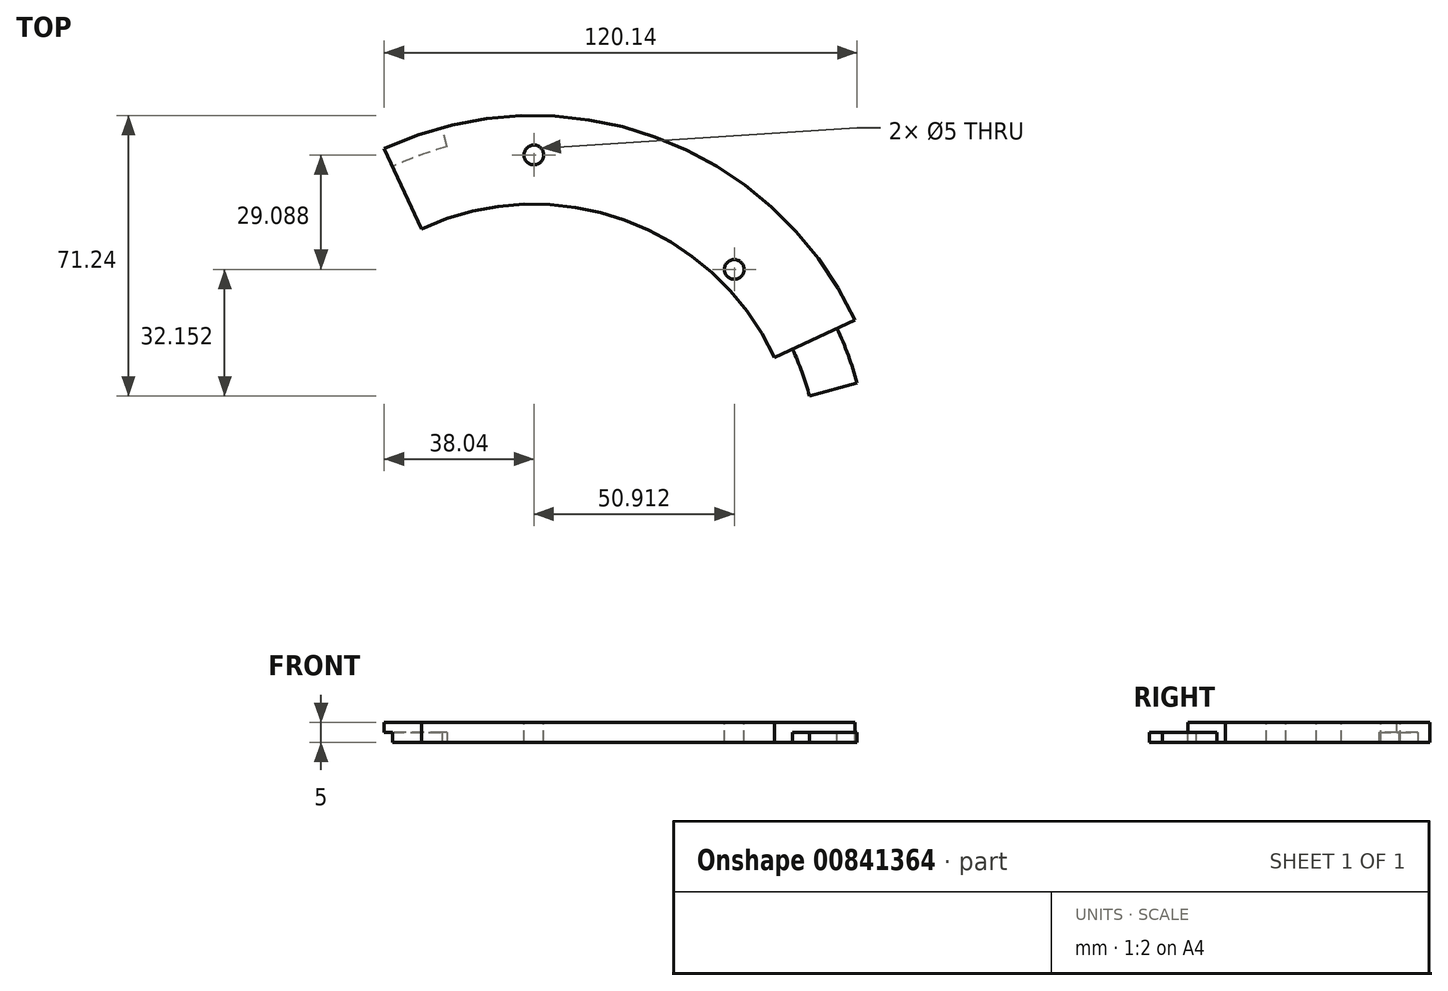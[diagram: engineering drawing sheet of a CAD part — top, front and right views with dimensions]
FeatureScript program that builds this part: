
annotation { "Feature Type Name" : "Feature", "Feature Type Description" : "" }
export const myFeature = defineFeature(function(context is Context, id is Id, definition is map)
    precondition{}
    {
        {
            var Q0;
            Q0=qCreatedBy(makeId("Top.planeOp"),FACE);
            var sketch = newSketch(context, id + "F0", { "sketchPlane" : qUnion([Q0])});
            skCircle(sketch, "E0", {"center": v(0, 0) * mm, "radius": 90 * mm});
            skSolve(sketch);
        }
        {
            var Q0;
            Q0 = qSketchRegion(id + "F0", true);
            extrude(context, id + "F1", {"entities" : qUnion([Q0]), "depth" : 5 * mm, "offsetDistance" : 25 * mm});
        }
        {
            var Q0;
            Q0=makeQuery(id+"F1.opExtrude","CAP_FACE",FACE,{"disambiguationData":[OSD([sQuery(id+"F0.wireOp",EDGE,"E0")])],"isStart":false});
            var sketch = newSketch(context, id + "F2", { "sketchPlane" : qUnion([Q0])});
            skCircle(sketch, "E1", {"center": v(0, 0) * mm, "radius": 67.5 * mm});
            skSolve(sketch);
        }
        {
            var Q0;
            Q0 = qSketchRegion(id + "F2", true);
            extrude(context, id + "F3", {"entities" : qUnion([Q0]), "operationType" : NewBodyOperationType.REMOVE, "oppositeDirection" : true, "depth" : 5 * mm, "offsetDistance" : 25 * mm});
        }
        {
            var Q0;
            Q0=makeQuery(id+"F1.opExtrude","CAP_FACE",FACE,{"disambiguationData":[OSD([sQuery(id+"F0.wireOp",EDGE,"E0")])],"isStart":false});
            var sketch = newSketch(context, id + "F4", { "sketchPlane" : qUnion([Q0])});
            skCircle(sketch, "E2", {"center": v(0, 80) * mm, "radius": 2.5 * mm});
            skSolve(sketch);
        }
        {
            var Q0;
            Q0 = qSketchRegion(id + "F4", true);
            extrude(context, id + "F5", {"entities" : qUnion([Q0]), "operationType" : NewBodyOperationType.REMOVE, "endBound" : BoundingType.THROUGH_ALL, "oppositeDirection" : true, "depth" : 25 * mm, "offsetDistance" : 25 * mm});
        }
        {
            var Q0;
            Q0=makeQuery(id+"F1.opExtrude","CAP_FACE",FACE,{"disambiguationData":[OSD([sQuery(id+"F0.wireOp",EDGE,"E0")])],"isStart":false});
            var sketch = newSketch(context, id + "F6", { "sketchPlane" : qUnion([Q0])});
            skCircle(sketch, "E3", {"center": v(50.91, 50.91) * mm, "radius": 2.5 * mm});
            skLineSegment(sketch, "E4", {"start": v(50.91, 50.91) * mm, "end": v(0, 0) * mm});
            skSolve(sketch);
        }
        {
            var Q0;
            Q0 = qSketchRegion(id + "F6", true);
            extrude(context, id + "F7", {"entities" : qUnion([Q0]), "operationType" : NewBodyOperationType.REMOVE, "endBound" : BoundingType.THROUGH_ALL, "oppositeDirection" : true, "depth" : 25 * mm, "offsetDistance" : 25 * mm});
        }
        {
            var Q0;
            Q0=makeQuery(id+"F1.opExtrude","CAP_FACE",FACE,{"disambiguationData":[OSD([sQuery(id+"F0.wireOp",EDGE,"E0")])],"isStart":false});
            var sketch = newSketch(context, id + "F8", { "sketchPlane" : qUnion([Q0])});
            skLineSegment(sketch, "E5", {"start": v(-38.04, 81.57) * mm, "end": v(-28.53, 61.18) * mm});
            skLineSegment(sketch, "E6", {"start": v(61.18, 28.53) * mm, "end": v(81.57, 38.04) * mm});
            skArc(sketch, "E7", {"start": v(-38.04, 81.57) * mm, "mid": v(-30.78, -84.57) * mm, "end": v(81.57, 38.04) * mm});
            skArc(sketch, "E8", {"start": v(-28.53, 61.18) * mm, "mid": v(-23.09, -63.43) * mm, "end": v(61.18, 28.53) * mm});
            skSolve(sketch);
        }
        {
            var Q0;
            Q0 = qSketchRegion(id + "F8", true);
            extrude(context, id + "F9", {"entities" : qUnion([Q0]), "operationType" : NewBodyOperationType.REMOVE, "oppositeDirection" : true, "depth" : 2.5 * mm, "offsetDistance" : 25 * mm});
        }
        {
            var Q0;
            Q0=makeQuery(id+"F9.boolean.opBoolean","COPY",FACE,{"derivedFrom":makeQuery(id+"F9.opExtrude","CAP_FACE",FACE,{"disambiguationData":[OSD([sQuery(id+"F8.wireOp",EDGE,"E5"),sQuery(id+"F8.wireOp",EDGE,"E6"),sQuery(id+"F8.wireOp",EDGE,"E7"),sQuery(id+"F8.wireOp",EDGE,"E8")])],"isStart":false})});
            var sketch = newSketch(context, id + "F10", { "sketchPlane" : qUnion([Q0])});
            skArc(sketch, "E9.0", {"start": v(-35.92, 77.04) * mm, "mid": v(-29.07, -79.87) * mm, "end": v(77.04, 35.92) * mm});
            skSolve(sketch);
        }
        {
            var Q0;
            {var subQ0=sQuery(id+"F10.wireOp",EDGE,"E9.0");Q0=makeQuery(id+"F10.imprint","IMPRINT",FACE,{"disambiguationData":[TD([[makeQuery(id+"F10.imprint","IMPRINT",EDGE,{"derivedFrom":subQ0}),-1.0]])]});}
            extrude(context, id + "F11", {"entities" : qUnion([Q0]), "operationType" : NewBodyOperationType.REMOVE, "endBound" : BoundingType.THROUGH_ALL, "oppositeDirection" : true, "depth" : 25 * mm, "offsetDistance" : 25 * mm});
        }
        {
            var Q0;
            Q0=makeQuery(id+"F9.boolean.opBoolean","COPY",FACE,{"derivedFrom":makeQuery(id+"F9.opExtrude","CAP_FACE",FACE,{"disambiguationData":[OSD([sQuery(id+"F8.wireOp",EDGE,"E5"),sQuery(id+"F8.wireOp",EDGE,"E6"),sQuery(id+"F8.wireOp",EDGE,"E7"),sQuery(id+"F8.wireOp",EDGE,"E8")])],"isStart":false})});
            var sketch = newSketch(context, id + "F12", { "sketchPlane" : qUnion([Q0])});
            skArc(sketch, "E10.0", {"start": v(-30.64, 65.7) * mm, "mid": v(-24.8, -68.13) * mm, "end": v(65.7, 30.64) * mm});
            skSolve(sketch);
        }
        {
            var Q0;
            {var subQ0=sQuery(id+"F12.wireOp",EDGE,"E10.0");Q0=makeQuery(id+"F12.imprint","IMPRINT",FACE,{"disambiguationData":[TD([[makeQuery(id+"F12.imprint","IMPRINT",EDGE,{"derivedFrom":subQ0}),1.0]])]});}
            extrude(context, id + "F13", {"entities" : qUnion([Q0]), "operationType" : NewBodyOperationType.REMOVE, "endBound" : BoundingType.THROUGH_ALL, "oppositeDirection" : true, "depth" : 25 * mm, "offsetDistance" : 25 * mm});
        }
        {
            var Q0;
            Q0=makeQuery(id+"F9.boolean.opBoolean","COPY",FACE,{"derivedFrom":makeQuery(id+"F9.opExtrude","CAP_FACE",FACE,{"disambiguationData":[OSD([sQuery(id+"F8.wireOp",EDGE,"E5"),sQuery(id+"F8.wireOp",EDGE,"E6"),sQuery(id+"F8.wireOp",EDGE,"E7"),sQuery(id+"F8.wireOp",EDGE,"E8")])],"isStart":false})});
            var sketch = newSketch(context, id + "F14", { "sketchPlane" : qUnion([Q0])});
            skLineSegment(sketch, "E11", {"start": v(0, 0) * mm, "end": v(98.66, 26.44) * mm});
            skLineSegment(sketch, "E12", {"start": v(98.66, 26.44) * mm, "end": v(88.85, -67.58) * mm});
            skLineSegment(sketch, "E13", {"start": v(88.85, -67.58) * mm, "end": v(32.12, -89.84) * mm});
            skLineSegment(sketch, "E14", {"start": v(32.12, -89.84) * mm, "end": v(-65.97, -85.6) * mm});
            skLineSegment(sketch, "E15", {"start": v(-65.97, -85.6) * mm, "end": v(-138.6, -33.64) * mm});
            skLineSegment(sketch, "E16", {"start": v(0, 0) * mm, "end": v(-50.34, 107.96) * mm});
            skLineSegment(sketch, "E17", {"start": v(-50.34, 107.96) * mm, "end": v(-138.6, -33.64) * mm});
            skSolve(sketch);
        }
        {
            var Q0;
            Q0 = qSketchRegion(id + "F14", true);
            extrude(context, id + "F15", {"entities" : qUnion([Q0]), "operationType" : NewBodyOperationType.REMOVE, "endBound" : BoundingType.THROUGH_ALL, "oppositeDirection" : true, "depth" : 25 * mm, "offsetDistance" : 25 * mm});
        }
        {
            var Q0;
            Q0=makeQuery(id+"F1.opExtrude","CAP_FACE",FACE,{"disambiguationData":[OSD([sQuery(id+"F0.wireOp",EDGE,"E0")])],"isStart":true});
            var sketch = newSketch(context, id + "F16", { "sketchPlane" : qUnion([Q0])});
            skArc(sketch, "E18.0", {"start": v(77.04, -35.92) * mm, "mid": v(29.07, -79.87) * mm, "end": v(-35.92, -77.04) * mm});
            skSolve(sketch);
        }
        {
            var Q0;
            {var subQ3=sQuery(id+"F16.wireOp",EDGE,"E18.0");Q0=makeQuery(id+"F16.imprint","IMPRINT",FACE,{"disambiguationData":[TD([[makeQuery(id+"F16.imprint","IMPRINT",EDGE,{"derivedFrom":subQ3}),-1.0]])]});}
            var sketch = newSketch(context, id + "F17", { "sketchPlane" : qUnion([Q0])});
            skArc(sketch, "E19.0", {"start": v(65.7, -30.64) * mm, "mid": v(24.8, -68.13) * mm, "end": v(-30.64, -65.7) * mm});
            skSolve(sketch);
        }
        {
            var Q0;
            {var subQ1=sQuery(id+"F16.wireOp",EDGE,"E18.0");var subQ2=makeQuery(id+"F16.imprint","IMPRINT",EDGE,{"derivedFrom":subQ1});Q0=makeQuery(id+"F17.imprint","IMPRINT",FACE,{"disambiguationData":[TD([[makeQuery(id+"F17.imprint","IMPRINT",EDGE,{"derivedFrom":subQ2}),-1.0]])]});}
            var sketch = newSketch(context, id + "F18", { "sketchPlane" : qUnion([Q0])});
            skLineSegment(sketch, "E20", {"start": v(0, 0) * mm, "end": v(-24.9, -92.95) * mm});
            skSolve(sketch);
        }
        {
            var Q0;
            {var subQ0=sQuery(id+"F18.wireOp",EDGE,"E20");var subQ6=sQuery(id+"F16.wireOp",EDGE,"E18.0");var subQ11=makeQuery(id+"F16.imprint","IMPRINT",EDGE,{"derivedFrom":subQ6});var subQ12=makeQuery(id+"F17.imprint","IMPRINT",EDGE,{"derivedFrom":subQ11});var subQ13=makeQuery(id+"F18.imprint","INTERSECT",VERTEX,{"derivedFrom":[subQ12,subQ0]});Q0=makeQuery(id+"F18.imprint","IMPRINT",FACE,{"disambiguationData":[TD([[makeQuery(id+"F18.imprint","IMPRINT",EDGE,{"disambiguationData":[TD([[subQ13,1.0]])],"derivedFrom":subQ0}),-1.0]])]});}
            extrude(context, id + "F19", {"entities" : qUnion([Q0]), "operationType" : NewBodyOperationType.REMOVE, "oppositeDirection" : true, "depth" : 2.5 * mm, "offsetDistance" : 25 * mm});
        }
    });
